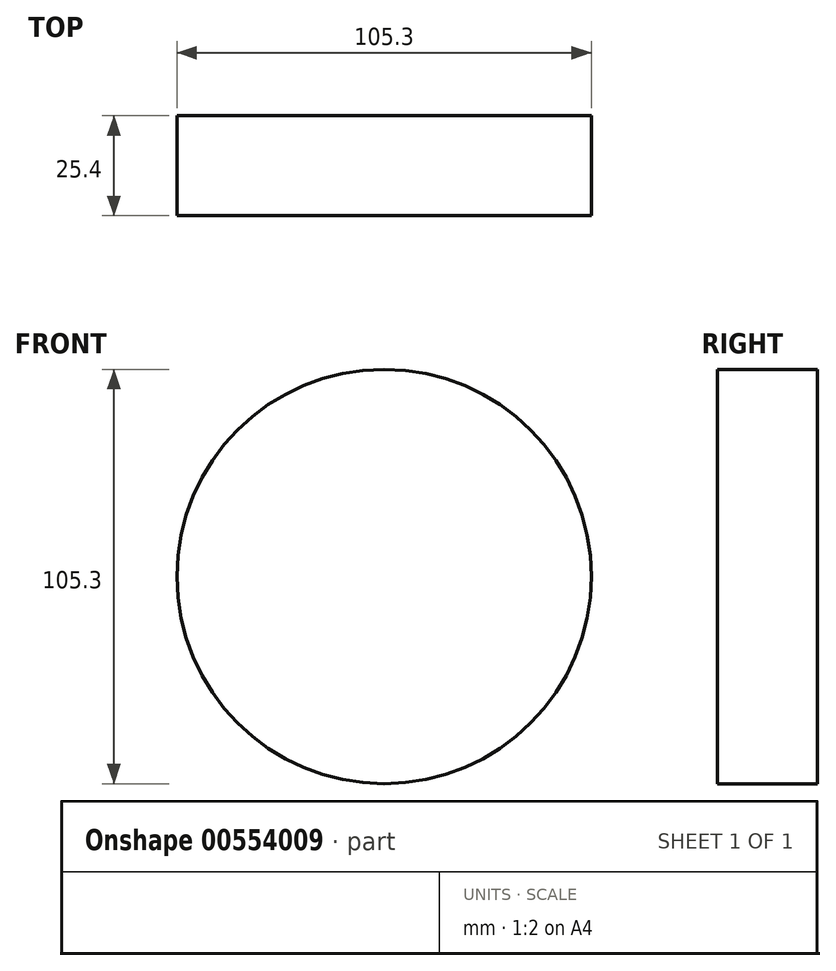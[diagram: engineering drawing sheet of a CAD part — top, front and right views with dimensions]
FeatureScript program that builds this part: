
annotation { "Feature Type Name" : "Feature", "Feature Type Description" : "" }
export const myFeature = defineFeature(function(context is Context, id is Id, definition is map)
    precondition{}
    {
        {
            var Q0;
            Q0=qCreatedBy(makeId("Front.planeOp"),FACE);
            var sketch = newSketch(context, id + "F0", { "sketchPlane" : qUnion([Q0])});
            skCircle(sketch, "E0", {"center": v(0, 0) * mm, "radius": 52.65 * mm});
            skSolve(sketch);
        }
        {
            var Q0;
            Q0 = qSketchRegion(id + "F0", true);
            extrude(context, id + "F1", {"entities" : qUnion([Q0]), "depth" : 25.4 * mm, "offsetDistance" : 25.4 * mm});
        }
    });
